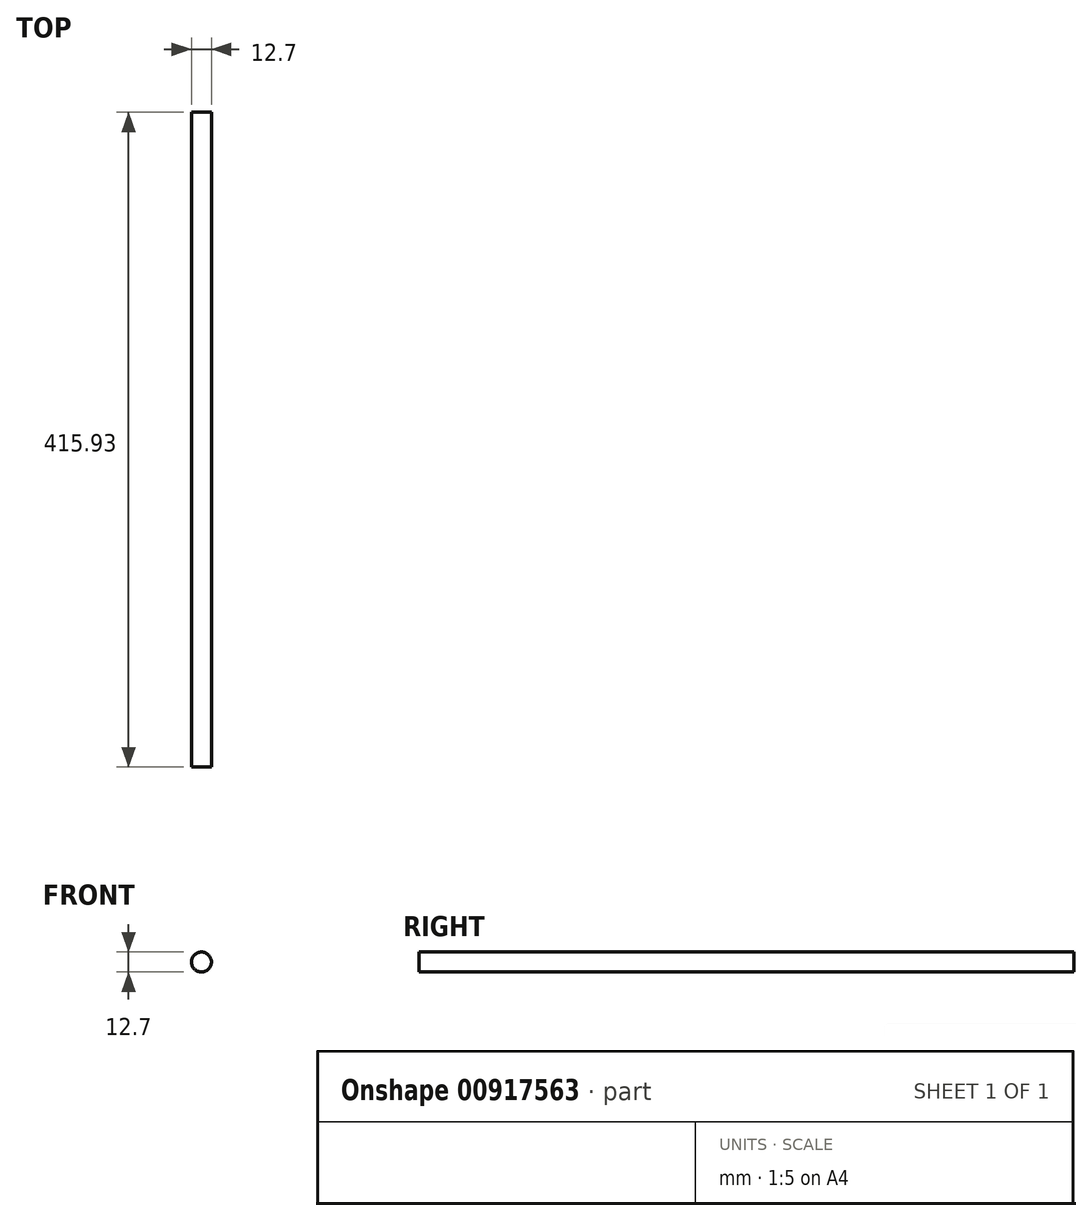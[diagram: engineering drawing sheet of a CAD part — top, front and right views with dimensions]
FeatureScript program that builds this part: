
annotation { "Feature Type Name" : "Feature", "Feature Type Description" : "" }
export const myFeature = defineFeature(function(context is Context, id is Id, definition is map)
    precondition{}
    {
        {
            var Q0;
            Q0=qCreatedBy(makeId("Front.planeOp"),FACE);
            var sketch = newSketch(context, id + "F0", { "sketchPlane" : qUnion([Q0])});
            skCircle(sketch, "E0", {"center": v(0, 0) * mm, "radius": 6.35 * mm});
            skSolve(sketch);
        }
        {
            var Q0;
            Q0=makeQuery(id+"F0.imprint","IMPRINT",FACE,{"disambiguationData":[TD([[makeQuery(id+"F0.imprint","IMPRINT",EDGE,{"derivedFrom":sQuery(id+"F0.wireOp",EDGE,"E0")}),1.0]])]});
            extrude(context, id + "F1", {"entities" : qUnion([Q0]), "depth" : 415.92 * mm, "offsetDistance" : 25.4 * mm});
        }
    });
